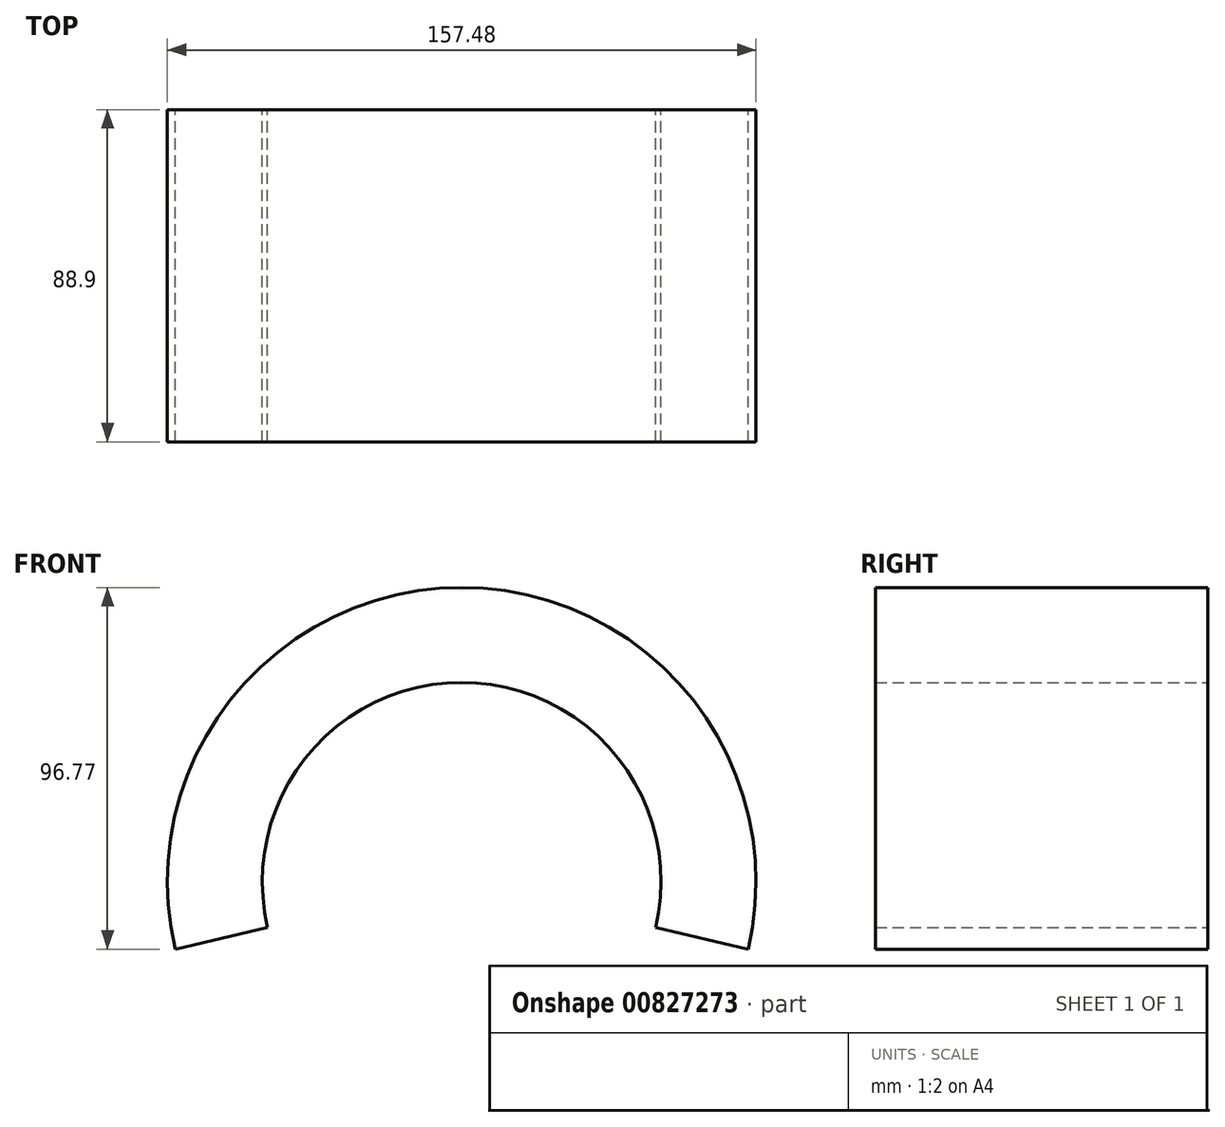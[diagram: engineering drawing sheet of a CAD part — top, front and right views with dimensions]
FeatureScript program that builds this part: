
annotation { "Feature Type Name" : "Feature", "Feature Type Description" : "" }
export const myFeature = defineFeature(function(context is Context, id is Id, definition is map)
    precondition{}
    {
        {
            var Q0;
            Q0=qCreatedBy(makeId("Front.planeOp"),FACE);
            var sketch = newSketch(context, id + "F0", { "sketchPlane" : qUnion([Q0])});
            skArc(sketch, "E0", {"start": v(0, 0) * mm, "mid": v(51.92, 65.55) * mm, "end": v(103.85, 0) * mm});
            skLineSegment(sketch, "E1", {"start": v(103.85, 0) * mm, "end": v(103.85, 0) * mm});
            skLineSegment(sketch, "E2", {"start": v(103.85, 0) * mm, "end": v(128.57, -5.82) * mm});
            skArc(sketch, "E3", {"start": v(128.57, -5.82) * mm, "mid": v(51.92, 90.95) * mm, "end": v(-24.73, -5.82) * mm});
            skLineSegment(sketch, "E4", {"start": v(-24.73, -5.82) * mm, "end": v(0, 0) * mm});
            skSolve(sketch);
        }
        {
            var Q0;
            Q0=makeQuery(id+"F0.imprint","IMPRINT",FACE,{"disambiguationData":[TD([[makeQuery(id+"F0.imprint","IMPRINT",EDGE,{"derivedFrom":sQuery(id+"F0.wireOp",EDGE,"E0")}),1.0]])]});
            var Q1;
            Q1 = qSketchRegion(id + "F0", true);
            extrude(context, id + "F1", {"entities" : qUnion([Q0, Q1]), "depth" : 88.9 * mm, "offsetDistance" : 25.4 * mm});
        }
    });
